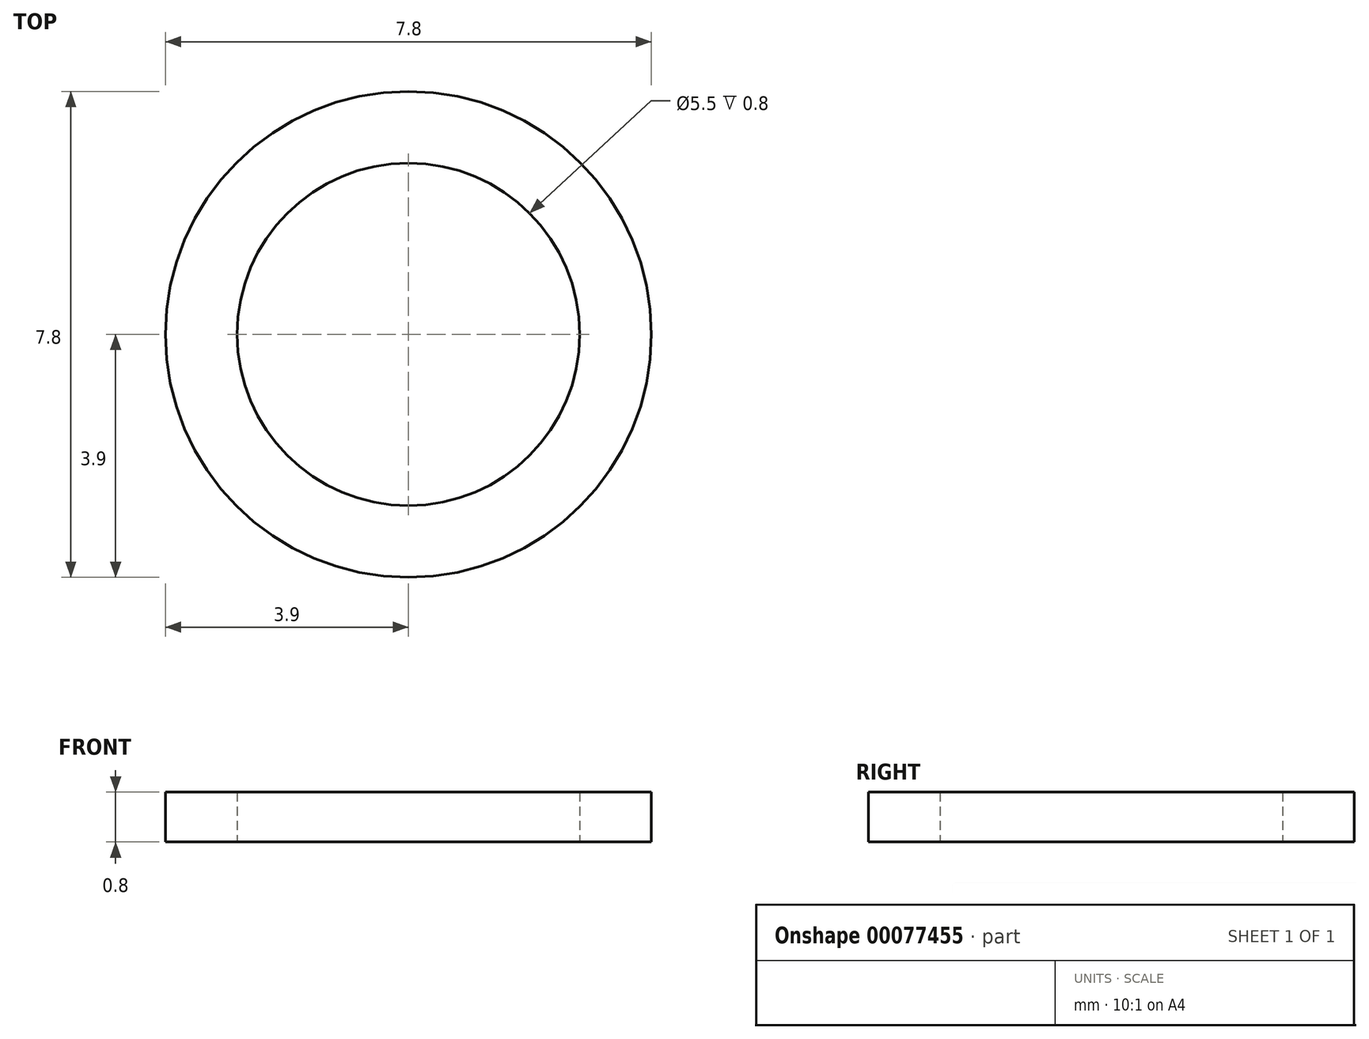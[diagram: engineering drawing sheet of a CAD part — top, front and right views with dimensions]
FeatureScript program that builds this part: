
annotation { "Feature Type Name" : "Feature", "Feature Type Description" : "" }
export const myFeature = defineFeature(function(context is Context, id is Id, definition is map)
    precondition{}
    {
        {
            var Q0;
            Q0=qCreatedBy(makeId("Top.planeOp"),FACE);
            var sketch = newSketch(context, id + "F0", { "sketchPlane" : qUnion([Q0])});
            skCircle(sketch, "E0", {"center": v(0, 0) * mm, "radius": 2.75 * mm});
            skCircle(sketch, "E1", {"center": v(0, 0) * mm, "radius": 3.9 * mm});
            skSolve(sketch);
        }
        {
            var Q0;
            Q0=makeQuery(id+"F0.imprint","IMPRINT",FACE,{"disambiguationData":[TD([[makeQuery(id+"F0.imprint","IMPRINT",EDGE,{"derivedFrom":sQuery(id+"F0.wireOp",EDGE,"E0")}),-1.0]])]});
            extrude(context, id + "F1", {"entities" : qUnion([Q0]), "depth" : 0.8 * mm});
        }
    });
